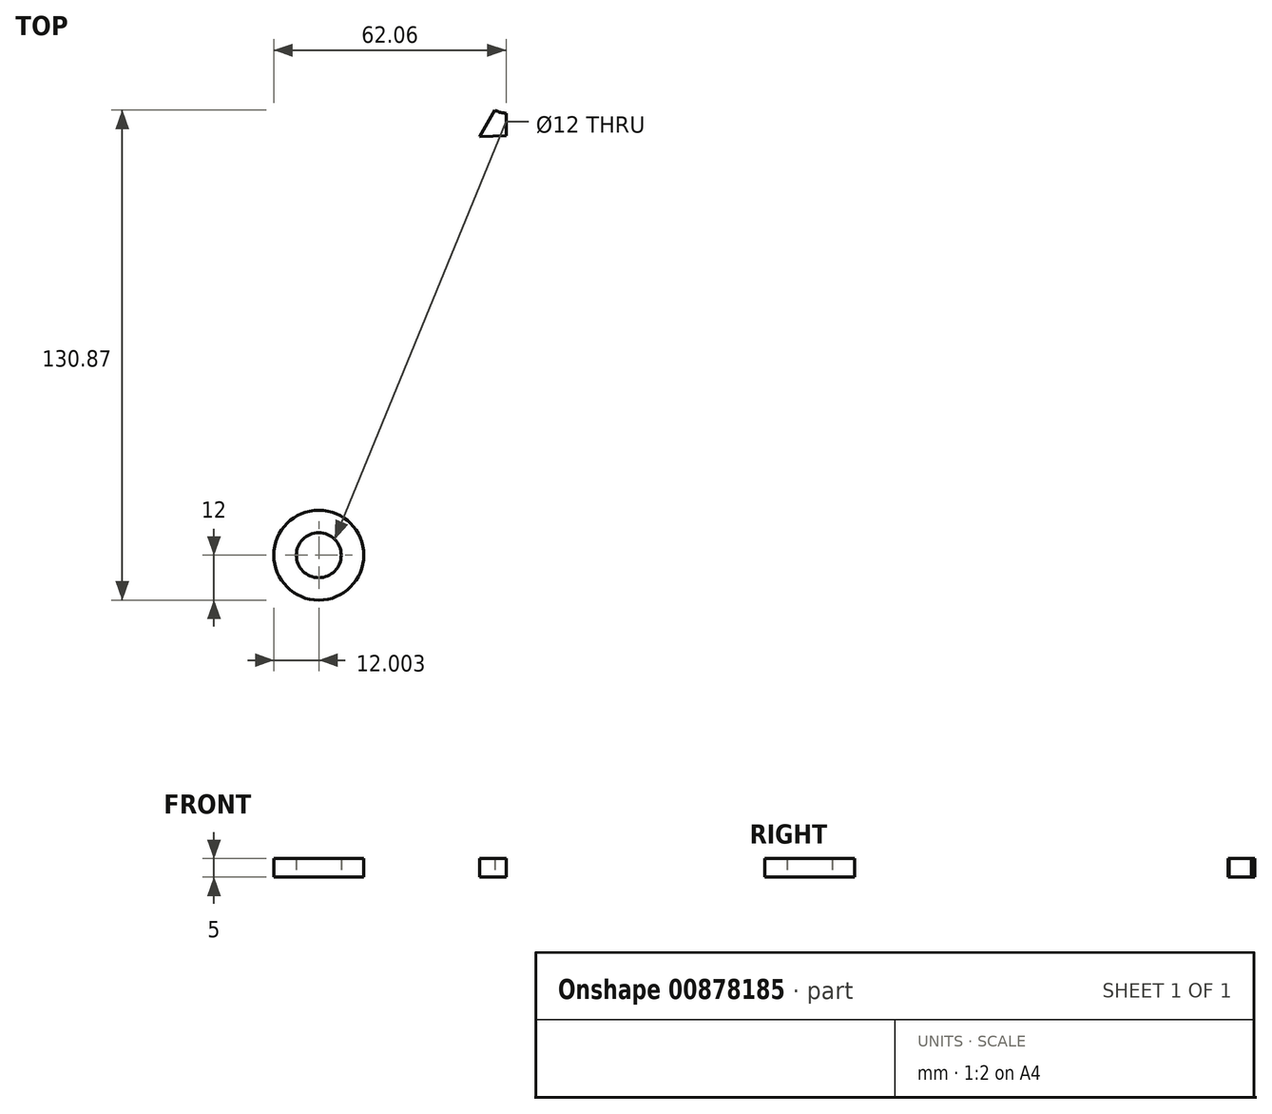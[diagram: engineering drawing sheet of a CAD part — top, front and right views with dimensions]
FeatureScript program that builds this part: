
annotation { "Feature Type Name" : "Feature", "Feature Type Description" : "" }
export const myFeature = defineFeature(function(context is Context, id is Id, definition is map)
    precondition{}
    {
        {
            var Q0;
            Q0=qCreatedBy(makeId("Top.planeOp"),FACE);
            var sketch = newSketch(context, id + "F0", { "sketchPlane" : qUnion([Q0])});
            skCircle(sketch, "E0", {"center": v(0, 0) * mm, "radius": 162 * mm, "construction": true});
            skLineSegment(sketch, "E1", {"start": v(-162, 0) * mm, "end": v(-116, 0) * mm, "construction": true});
            skLineSegment(sketch, "E2", {"start": v(-116, 0) * mm, "end": v(-70, 0) * mm, "construction": true});
            skCircle(sketch, "E3", {"center": v(0, 0) * mm, "radius": 70 * mm, "construction": true});
            skLineSegment(sketch, "E4", {"start": v(-34.34, 61) * mm, "end": v(-34.34, -61) * mm, "construction": true});
            skCircle(sketch, "E5", {"center": v(0, 0) * mm, "radius": 65 * mm, "construction": true});
            skLineSegment(sketch, "E6", {"start": v(-46.66, -45.25) * mm, "end": v(15.72, 63.07) * mm});
            skCircle(sketch, "E7", {"center": v(15.72, 63.07) * mm, "radius": 6 * mm});
            skCircle(sketch, "E8", {"center": v(-46.66, -45.25) * mm, "radius": 6 * mm});
            skCircle(sketch, "E9", {"center": v(-34.34, -61) * mm, "radius": 6 * mm});
            skCircle(sketch, "E10", {"center": v(-34.34, 61) * mm, "radius": 6 * mm});
            skLineSegment(sketch, "E11", {"start": v(-34.34, -61) * mm, "end": v(-34.34, -67) * mm, "construction": true});
            skLineSegment(sketch, "E12", {"start": v(-34.34, -61) * mm, "end": v(-28.34, -61) * mm});
            skArc(sketch, "E13", {"start": v(-58.58, -43.86) * mm, "mid": v(-58.22, -48.5) * mm, "end": v(-56.11, -52.65) * mm});
            skArc(sketch, "E14", {"start": v(-43.79, -68.4) * mm, "mid": v(-23.55, -66.26) * mm, "end": v(-34.34, -49) * mm, "construction": true});
            skArc(sketch, "E15", {"start": v(-34.83, 72.99) * mm, "mid": v(-43, 69.3) * mm, "end": v(-46.34, 61) * mm});
            skArc(sketch, "E16", {"start": v(15.72, 51.07) * mm, "mid": v(27.71, 63.56) * mm, "end": v(14.73, 75.03) * mm});
            skLineSegment(sketch, "E17", {"start": v(15.72, 63.07) * mm, "end": v(15.72, 75.07) * mm, "construction": true});
            skLineSegment(sketch, "E18", {"start": v(15.72, 75.07) * mm, "end": v(-34.83, 72.99) * mm});
            skLineSegment(sketch, "E19", {"start": v(-34.34, 61) * mm, "end": v(-28.34, 61) * mm});
            skLineSegment(sketch, "E20", {"start": v(-22.34, 61) * mm, "end": v(-22.34, -61) * mm});
            skLineSegment(sketch, "E21", {"start": v(-34.34, 61) * mm, "end": v(-46.34, 61) * mm});
            skLineSegment(sketch, "E22", {"start": v(-46.34, 61) * mm, "end": v(-58.58, -43.86) * mm});
            skLineSegment(sketch, "E23", {"start": v(-60.46, -47.09) * mm, "end": v(-43.48, -68.78) * mm});
            skCircle(sketch, "E24", {"center": v(-34.34, -61) * mm, "radius": 12 * mm});
            skLineSegment(sketch, "E25", {"start": v(15.72, 63.07) * mm, "end": v(15.72, 51.07) * mm});
            skLineSegment(sketch, "E26", {"start": v(15.72, 51.07) * mm, "end": v(-22.34, 49.49) * mm});
            skLineSegment(sketch, "E27.trimOffspring", {"start": v(-22.45, 61) * mm, "end": v(-22.34, 61) * mm});
            skArc(sketch, "E28.trimOffspring", {"start": v(-22.34, 61) * mm, "mid": v(-22.34, 61.02) * mm, "end": v(-22.34, 61.04) * mm});
            skArc(sketch, "E29.trimOffspring", {"start": v(-40.6, -50.76) * mm, "mid": v(-43.73, -53.53) * mm, "end": v(-45.72, -57.21) * mm, "construction": true});
            skLineSegment(sketch, "E30", {"start": v(52.02, 38.97) * mm, "end": v(12.68, -63.75) * mm});
            skSolve(sketch);
        }
        {
            var Q0;
            Q0=makeQuery(id+"F0.imprint","IMPRINT",FACE,{"disambiguationData":[TD([[makeQuery(id+"F0.imprint","IMPRINT",EDGE,{"derivedFrom":sQuery(id+"F0.wireOp",EDGE,"E7")}),-1.0]])]});
            var Q1;
            Q1=makeQuery(id+"F0.imprint","IMPRINT",FACE,{"disambiguationData":[TD([[makeQuery(id+"F0.imprint","IMPRINT",EDGE,{"derivedFrom":sQuery(id+"F0.wireOp",EDGE,"E9")}),-1.0]])]});
            extrude(context, id + "F1", {"entities" : qUnion([Q0, Q1]), "depth" : 5 * mm, "offsetDistance" : 25 * mm});
        }
    });
